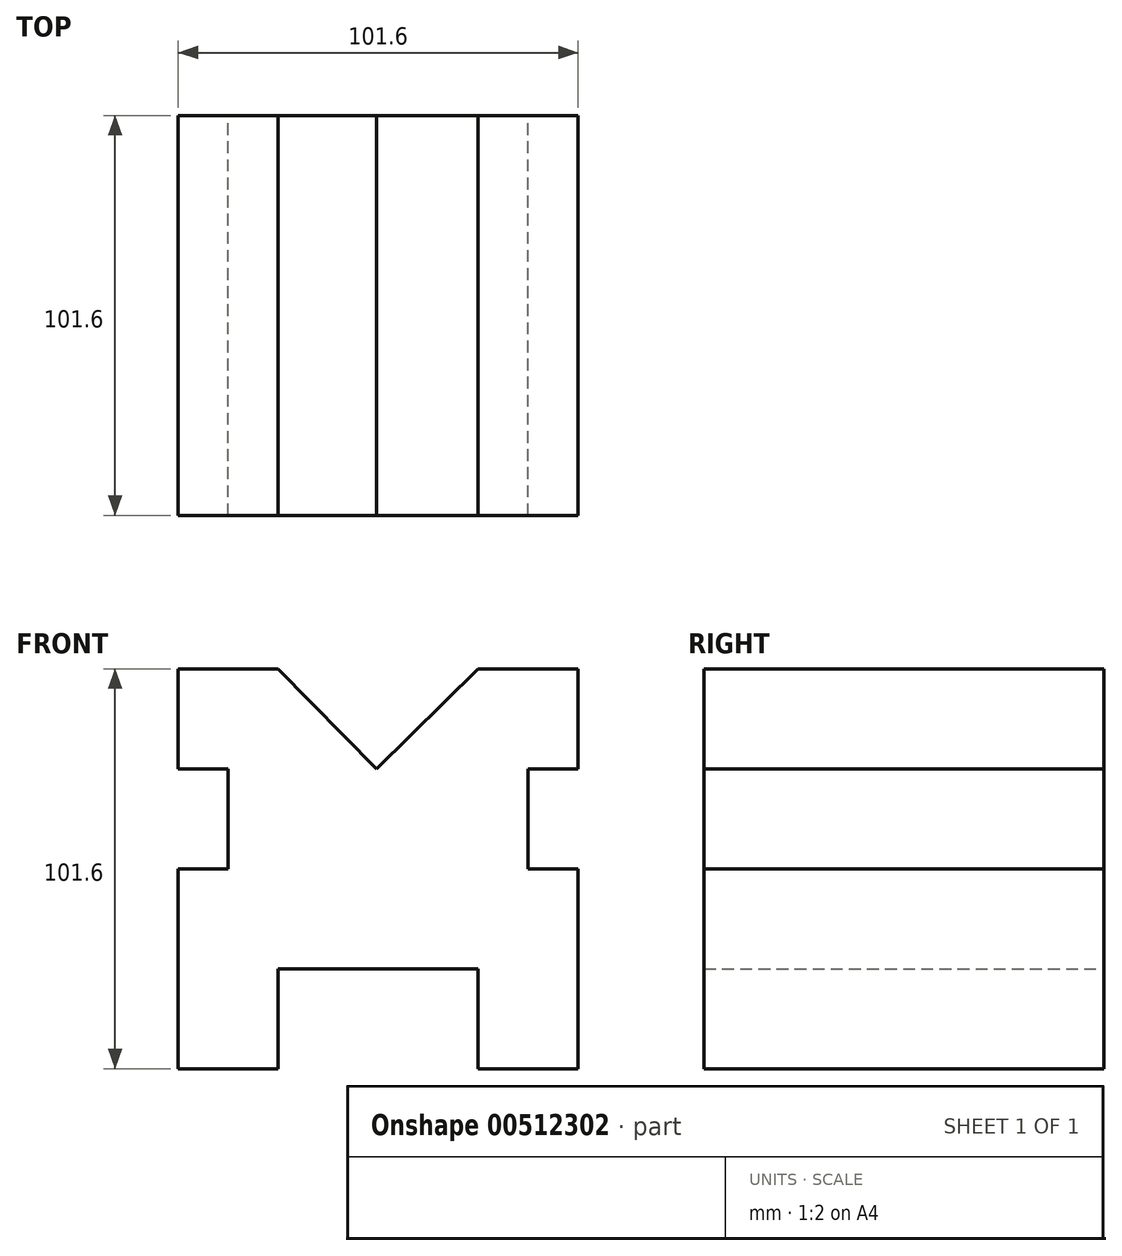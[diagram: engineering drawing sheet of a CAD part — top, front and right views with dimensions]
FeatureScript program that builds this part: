
annotation { "Feature Type Name" : "Feature", "Feature Type Description" : "" }
export const myFeature = defineFeature(function(context is Context, id is Id, definition is map)
    precondition{}
    {
        {
            var Q0;
            Q0=qCreatedBy(makeId("Front.planeOp"),FACE);
            var sketch = newSketch(context, id + "F0", { "sketchPlane" : qUnion([Q0])});
            skLineSegment(sketch, "E0", {"start": v(0, 0) * mm, "end": v(0, 50.8) * mm});
            skLineSegment(sketch, "E1", {"start": v(0, 50.8) * mm, "end": v(-12.7, 50.8) * mm});
            skLineSegment(sketch, "E2", {"start": v(-12.7, 50.8) * mm, "end": v(-12.7, 76.2) * mm});
            skLineSegment(sketch, "E3", {"start": v(-12.7, 76.2) * mm, "end": v(0, 76.2) * mm});
            skLineSegment(sketch, "E4", {"start": v(0, 76.2) * mm, "end": v(0, 101.6) * mm});
            skLineSegment(sketch, "E5", {"start": v(0, 0) * mm, "end": v(-25.4, 0) * mm});
            skLineSegment(sketch, "E6", {"start": v(-25.4, 0) * mm, "end": v(-25.4, 25.4) * mm});
            skLineSegment(sketch, "E7", {"start": v(-25.4, 25.4) * mm, "end": v(-76.2, 25.4) * mm});
            skLineSegment(sketch, "E8", {"start": v(-76.2, 25.4) * mm, "end": v(-76.2, 0) * mm});
            skLineSegment(sketch, "E9", {"start": v(-76.2, 0) * mm, "end": v(-101.6, 0) * mm});
            skLineSegment(sketch, "E10", {"start": v(-101.6, 0) * mm, "end": v(-101.6, 50.8) * mm});
            skLineSegment(sketch, "E11", {"start": v(-101.6, 50.8) * mm, "end": v(-88.9, 50.8) * mm});
            skLineSegment(sketch, "E12", {"start": v(-88.9, 50.8) * mm, "end": v(-88.9, 76.2) * mm});
            skLineSegment(sketch, "E13", {"start": v(-88.9, 76.2) * mm, "end": v(-101.6, 76.2) * mm});
            skLineSegment(sketch, "E14", {"start": v(-101.6, 76.2) * mm, "end": v(-101.6, 101.6) * mm});
            skLineSegment(sketch, "E15", {"start": v(-101.6, 101.6) * mm, "end": v(-76.2, 101.6) * mm});
            skLineSegment(sketch, "E16", {"start": v(0, 101.6) * mm, "end": v(-25.4, 101.6) * mm});
            skLineSegment(sketch, "E17", {"start": v(-76.2, 101.6) * mm, "end": v(-51.18, 76.2) * mm});
            skLineSegment(sketch, "E18", {"start": v(-51.18, 76.2) * mm, "end": v(-25.4, 101.6) * mm});
            skSolve(sketch);
        }
        {
            var Q0;
            Q0=makeQuery(id+"F0.imprint","IMPRINT",FACE,{"disambiguationData":[TD([[makeQuery(id+"F0.imprint","IMPRINT",EDGE,{"derivedFrom":sQuery(id+"F0.wireOp",EDGE,"E0")}),1.0]])]});
            extrude(context, id + "F1", {"entities" : qUnion([Q0]), "depth" : 101.6 * mm});
        }
    });
